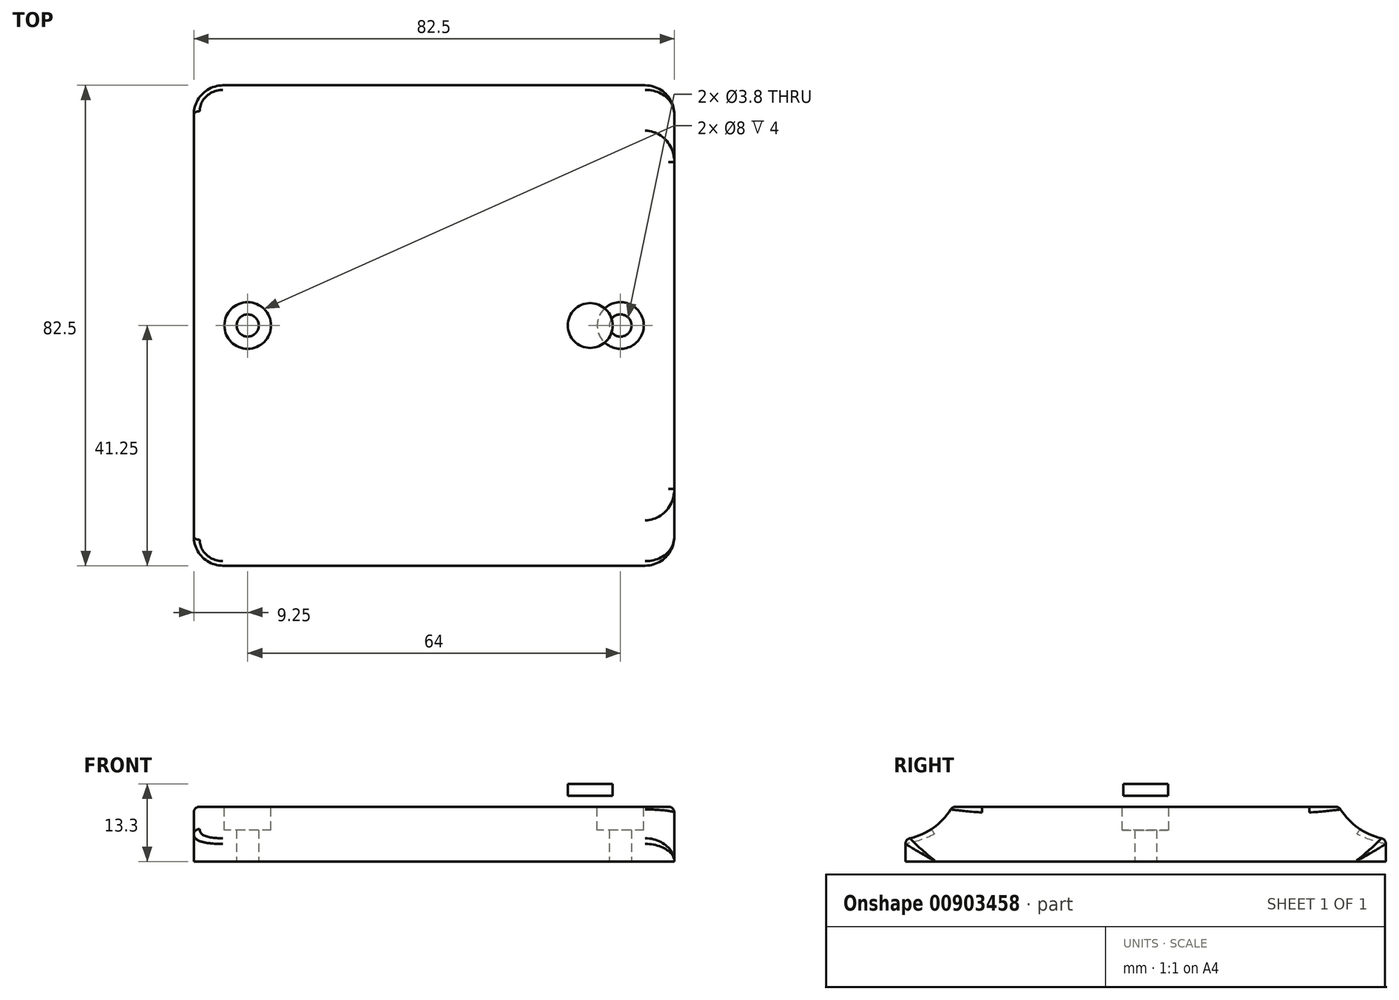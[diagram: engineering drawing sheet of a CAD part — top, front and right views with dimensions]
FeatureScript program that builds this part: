
annotation { "Feature Type Name" : "Feature", "Feature Type Description" : "" }
export const myFeature = defineFeature(function(context is Context, id is Id, definition is map)
    precondition{}
    {
        {
            var Q0;
            Q0=qCreatedBy(makeId("Top.planeOp"),FACE);
            var sketch = newSketch(context, id + "F0", { "sketchPlane" : qUnion([Q0])});
            skLineSegment(sketch, "E0.bottom", {"start": v(-41.25, 41.25) * mm, "end": v(41.25, 41.25) * mm});
            skLineSegment(sketch, "E0.top", {"start": v(-41.25, -41.25) * mm, "end": v(41.25, -41.25) * mm});
            skLineSegment(sketch, "E0.left", {"start": v(-41.25, 41.25) * mm, "end": v(-41.25, -41.25) * mm});
            skLineSegment(sketch, "E0.right", {"start": v(41.25, 41.25) * mm, "end": v(41.25, -41.25) * mm});
            skLineSegment(sketch, "E1", {"start": v(-41.25, 41.25) * mm, "end": v(41.25, -41.25) * mm, "construction": true});
            skLineSegment(sketch, "E2", {"start": v(41.25, 41.25) * mm, "end": v(-41.25, -41.25) * mm, "construction": true});
            skSolve(sketch);
        }
        {
            var Q0;
            Q0 = qSketchRegion(id + "F0", true);
            extrude(context, id + "F1", {"entities" : qUnion([Q0]), "depth" : 9.4 * mm, "offsetDistance" : 25 * mm});
        }
        {
            var Q0;
            Q0=makeQuery(id+"F1.opExtrude","SWEPT_FACE",FACE,{"disambiguationData":[OSD([sQuery(id+"F0.wireOp",EDGE,"E0.right")])]});
            var sketch = newSketch(context, id + "F2", { "sketchPlane" : qUnion([Q0])});
            skLineSegment(sketch, "E3", {"start": v(-46.6, 15) * mm, "end": v(67.18, 15) * mm, "construction": true});
            skLineSegment(sketch, "E4", {"start": v(43, 44.6) * mm, "end": v(43, -16.49) * mm, "construction": true});
            skCircle(sketch, "E5", {"center": v(43, 15) * mm, "radius": 11.3 * mm});
            skCircle(sketch, "E6.MirrorC", {"center": v(-43, 15) * mm, "radius": 11.3 * mm});
            skSolve(sketch);
        }
        {
            var Q0;
            Q0 = qSketchRegion(id + "F2", true);
            extrude(context, id + "F3", {"entities" : qUnion([Q0]), "operationType" : NewBodyOperationType.REMOVE, "oppositeDirection" : true, "depth" : 85 * mm, "offsetDistance" : 25 * mm});
        }
        {
            var Q0;
            Q0=makeQuery(id+"F3.boolean.opBoolean","INTERSECT",EDGE,{"derivedFrom":[makeQuery(id+"F1.opExtrude","SWEPT_FACE",FACE,{"disambiguationData":[OSD([sQuery(id+"F0.wireOp",EDGE,"E0.top")])]}),makeQuery(id+"F3.opExtrude","SWEPT_FACE",FACE,{"disambiguationData":[OSD([sQuery(id+"F2.wireOp",EDGE,"E6.MirrorC")])]})]});
            var Q1;
            Q1=makeQuery(id+"F3.boolean.opBoolean","INTERSECT",EDGE,{"derivedFrom":[makeQuery(id+"F1.opExtrude","CAP_FACE",FACE,{"disambiguationData":[OSD([sQuery(id+"F0.wireOp",EDGE,"E0.bottom"),sQuery(id+"F0.wireOp",EDGE,"E0.top"),sQuery(id+"F0.wireOp",EDGE,"E0.left"),sQuery(id+"F0.wireOp",EDGE,"E0.right")])],"isStart":false}),makeQuery(id+"F3.opExtrude","SWEPT_FACE",FACE,{"disambiguationData":[OSD([sQuery(id+"F2.wireOp",EDGE,"E6.MirrorC")])]})]});
            var Q2;
            Q2=makeQuery(id+"F3.boolean.opBoolean","INTERSECT",EDGE,{"derivedFrom":[makeQuery(id+"F1.opExtrude","CAP_FACE",FACE,{"disambiguationData":[OSD([sQuery(id+"F0.wireOp",EDGE,"E0.bottom"),sQuery(id+"F0.wireOp",EDGE,"E0.top"),sQuery(id+"F0.wireOp",EDGE,"E0.left"),sQuery(id+"F0.wireOp",EDGE,"E0.right")])],"isStart":false}),makeQuery(id+"F3.opExtrude","SWEPT_FACE",FACE,{"disambiguationData":[OSD([sQuery(id+"F2.wireOp",EDGE,"E5")])]})]});
            var Q3;
            Q3=makeQuery(id+"F3.boolean.opBoolean","INTERSECT",EDGE,{"derivedFrom":[makeQuery(id+"F1.opExtrude","SWEPT_FACE",FACE,{"disambiguationData":[OSD([sQuery(id+"F0.wireOp",EDGE,"E0.bottom")])]}),makeQuery(id+"F3.opExtrude","SWEPT_FACE",FACE,{"disambiguationData":[OSD([sQuery(id+"F2.wireOp",EDGE,"E5")])]})]});
            var Q4;
            Q4=makeQuery(id+"F1.opExtrude","CAP_EDGE",EDGE,{"disambiguationData":[OSD([sQuery(id+"F0.wireOp",EDGE,"E0.right")])],"isStart":false});
            var Q5;
            Q5=makeQuery(id+"F3.boolean.opBoolean","COPY",EDGE,{"derivedFrom":makeQuery(id+"F3.opExtrude","CAP_EDGE",EDGE,{"disambiguationData":[OSD([sQuery(id+"F2.wireOp",EDGE,"E5")])],"isStart":true})});
            var Q6;
            Q6=makeQuery(id+"F3.boolean.opBoolean","COPY",EDGE,{"derivedFrom":makeQuery(id+"F3.opExtrude","CAP_EDGE",EDGE,{"disambiguationData":[OSD([sQuery(id+"F2.wireOp",EDGE,"E6.MirrorC")])],"isStart":true})});
            var Q7;
            Q7=makeQuery(id+"F1.opExtrude","CAP_EDGE",EDGE,{"disambiguationData":[OSD([sQuery(id+"F0.wireOp",EDGE,"E0.left")])],"isStart":false});
            var Q8;
            Q8=makeQuery(id+"F3.boolean.opBoolean","INTERSECT",EDGE,{"derivedFrom":[makeQuery(id+"F1.opExtrude","SWEPT_FACE",FACE,{"disambiguationData":[OSD([sQuery(id+"F0.wireOp",EDGE,"E0.left")])]}),makeQuery(id+"F3.opExtrude","SWEPT_FACE",FACE,{"disambiguationData":[OSD([sQuery(id+"F2.wireOp",EDGE,"E5")])]})]});
            var Q9;
            Q9=makeQuery(id+"F3.boolean.opBoolean","INTERSECT",EDGE,{"derivedFrom":[makeQuery(id+"F1.opExtrude","SWEPT_FACE",FACE,{"disambiguationData":[OSD([sQuery(id+"F0.wireOp",EDGE,"E0.left")])]}),makeQuery(id+"F3.opExtrude","SWEPT_FACE",FACE,{"disambiguationData":[OSD([sQuery(id+"F2.wireOp",EDGE,"E6.MirrorC")])]})]});
            fillet(context, id + "F4", {"entities" : qUnion([Q0, Q1, Q2, Q3, Q4, Q5, Q6, Q7, Q8, Q9]), "radius" : 1 * mm, "tangentPropagation" : true, "allowEdgeOverflow" : false});
        }
        {
            var Q0;
            Q0=makeQuery(id+"F1.opExtrude","SWEPT_EDGE",EDGE,{"disambiguationData":[OSD([sQuery(id+"F0.wireOp",EDGE,"E0.top"),sQuery(id+"F0.wireOp",EDGE,"E0.left")])]});
            var Q1;
            Q1=makeQuery(id+"F1.opExtrude","SWEPT_EDGE",EDGE,{"disambiguationData":[OSD([sQuery(id+"F0.wireOp",EDGE,"E0.top"),sQuery(id+"F0.wireOp",EDGE,"E0.right")])]});
            var Q2;
            Q2=makeQuery(id+"F1.opExtrude","SWEPT_EDGE",EDGE,{"disambiguationData":[OSD([sQuery(id+"F0.wireOp",EDGE,"E0.bottom"),sQuery(id+"F0.wireOp",EDGE,"E0.right")])]});
            var Q3;
            Q3=makeQuery(id+"F1.opExtrude","SWEPT_EDGE",EDGE,{"disambiguationData":[OSD([sQuery(id+"F0.wireOp",EDGE,"E0.bottom"),sQuery(id+"F0.wireOp",EDGE,"E0.left")])]});
            fillet(context, id + "F5", {"entities" : qUnion([Q0, Q1, Q2, Q3]), "radius" : 5 * mm, "tangentPropagation" : true, "allowEdgeOverflow" : false});
        }
        {
            var Q0;
            Q0=qCreatedBy(makeId("Top.planeOp"),FACE);
            var sketch = newSketch(context, id + "F6", { "sketchPlane" : qUnion([Q0])});
            skCircle(sketch, "E7", {"center": v(32, 0) * mm, "radius": 1.9 * mm});
            skCircle(sketch, "E8.MirrorC", {"center": v(-32, 0) * mm, "radius": 1.9 * mm});
            skSolve(sketch);
        }
        {
            var Q0;
            Q0 = qSketchRegion(id + "F6", true);
            extrude(context, id + "F7", {"entities" : qUnion([Q0]), "operationType" : NewBodyOperationType.REMOVE, "endBound" : BoundingType.THROUGH_ALL, "depth" : 25 * mm, "offsetDistance" : 25 * mm});
        }
        {
            var Q0;
            Q0=makeQuery(id+"F1.opExtrude","CAP_FACE",FACE,{"disambiguationData":[OSD([sQuery(id+"F0.wireOp",EDGE,"E0.bottom"),sQuery(id+"F0.wireOp",EDGE,"E0.top"),sQuery(id+"F0.wireOp",EDGE,"E0.left"),sQuery(id+"F0.wireOp",EDGE,"E0.right")])],"isStart":false});
            var sketch = newSketch(context, id + "F8", { "sketchPlane" : qUnion([Q0])});
            skCircle(sketch, "E9", {"center": v(32, 0) * mm, "radius": 4 * mm});
            skCircle(sketch, "E10.MirrorC", {"center": v(-32, 0) * mm, "radius": 4 * mm});
            skSolve(sketch);
        }
        {
            var Q0;
            Q0 = qSketchRegion(id + "F8", true);
            extrude(context, id + "F9", {"entities" : qUnion([Q0]), "operationType" : NewBodyOperationType.REMOVE, "oppositeDirection" : true, "depth" : 4 * mm, "offsetDistance" : 25 * mm});
        }
        {
            var Q0;
            Q0=qCreatedBy(makeId("Top.planeOp"),FACE);
            cPlane(context, id + "F10", {"entities" : qUnion([Q0]), "cplaneType" : CPlaneType.OFFSET, "offset" : 13.3 * mm, "width" : 150 * mm, "height" : 150 * mm});
        }
        {
            var Q0;
            Q0=qCreatedBy(id+"F10.planeOp",FACE);
            var sketch = newSketch(context, id + "F11", { "sketchPlane" : qUnion([Q0])});
            skCircle(sketch, "E11", {"center": v(26.8, 0) * mm, "radius": 3.85 * mm});
            skSolve(sketch);
        }
        {
            var Q0;
            Q0 = qSketchRegion(id + "F11", true);
            extrude(context, id + "F12", {"entities" : qUnion([Q0]), "oppositeDirection" : true, "depth" : 2 * mm, "offsetDistance" : 25 * mm});
        }
    });
